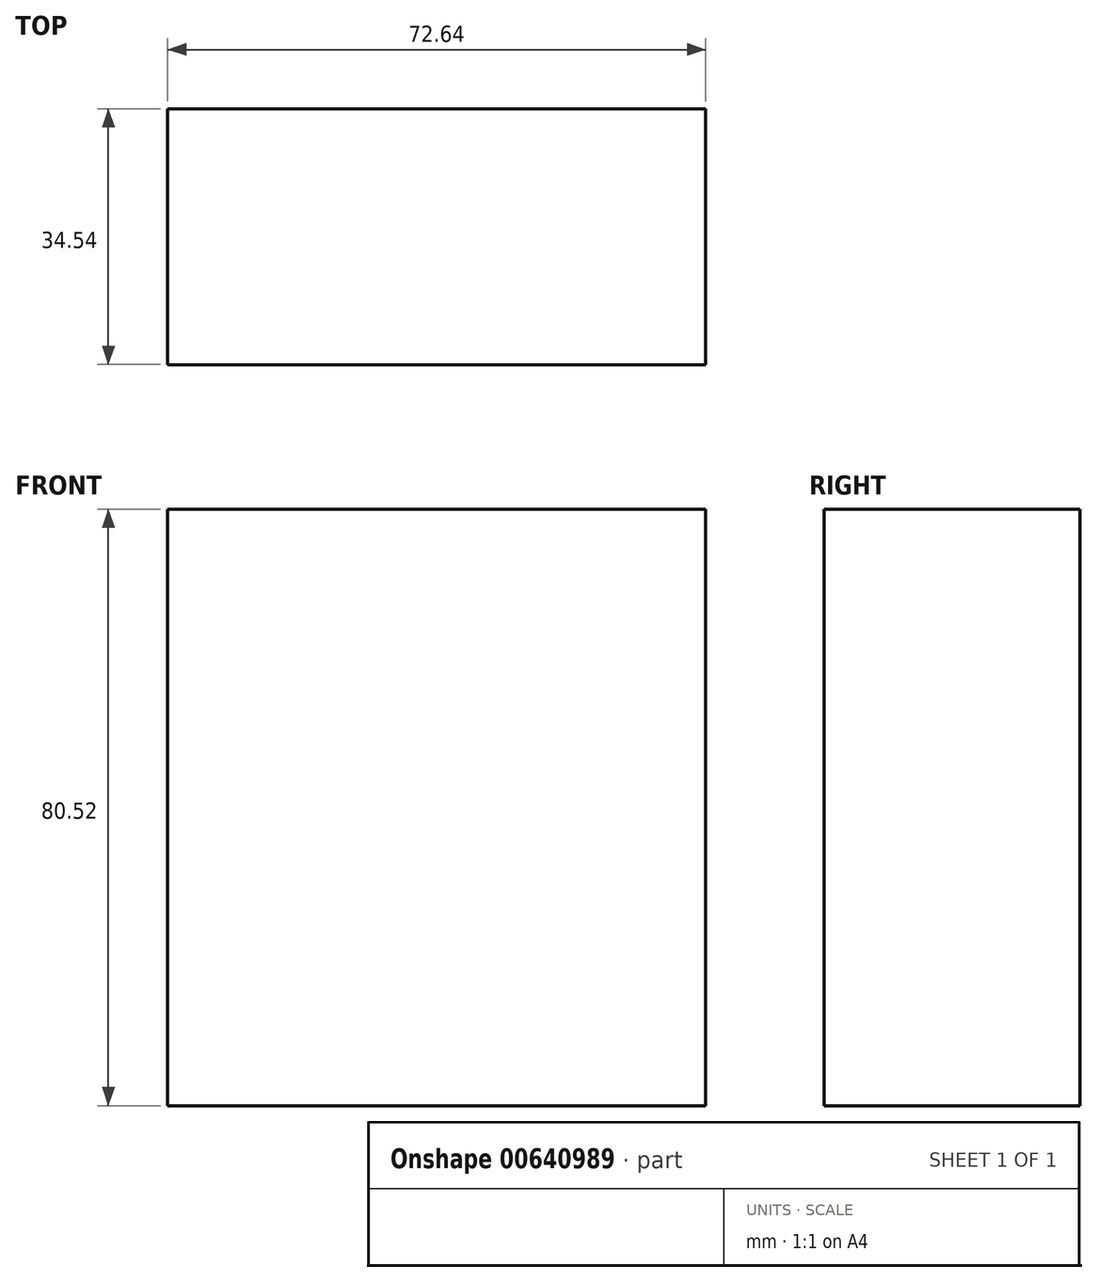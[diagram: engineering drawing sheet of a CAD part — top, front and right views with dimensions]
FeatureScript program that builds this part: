
annotation { "Feature Type Name" : "Feature", "Feature Type Description" : "" }
export const myFeature = defineFeature(function(context is Context, id is Id, definition is map)
    precondition{}
    {
        {
            var Q0;
            Q0=qCreatedBy(makeId("Front.planeOp"),FACE);
            var sketch = newSketch(context, id + "F0", { "sketchPlane" : qUnion([Q0])});
            skLineSegment(sketch, "E0.bottom", {"start": v(36.32, 40.26) * mm, "end": v(-36.32, 40.26) * mm});
            skLineSegment(sketch, "E0.top", {"start": v(36.32, -40.26) * mm, "end": v(-36.32, -40.26) * mm});
            skLineSegment(sketch, "E0.left", {"start": v(36.32, 40.26) * mm, "end": v(36.32, -40.26) * mm});
            skLineSegment(sketch, "E0.right", {"start": v(-36.32, 40.26) * mm, "end": v(-36.32, -40.26) * mm});
            skPoint(sketch, "E0.middle", {"position": v(0, 0) * mm});
            skSolve(sketch);
        }
        {
            var Q0;
            Q0=makeQuery(id+"F0.imprint","IMPRINT",FACE,{"disambiguationData":[TD([[makeQuery(id+"F0.imprint","IMPRINT",EDGE,{"derivedFrom":sQuery(id+"F0.wireOp",EDGE,"E0.bottom")}),1.0]])]});
            var Q1;
            Q1=sQuery(id+"F0.wireOp",EDGE,"E0.right");
            var Q2;
            Q2=sQuery(id+"F0.wireOp",EDGE,"E0.bottom");
            var Q3;
            Q3=sQuery(id+"F0.wireOp",EDGE,"E0.left");
            var Q4;
            Q4=sQuery(id+"F0.wireOp",EDGE,"E0.top");
            extrude(context, id + "F1", {"entities" : qUnion([Q0]), "surfaceEntities" : qUnion([Q1, Q2, Q3, Q4]), "depth" : 34.54 * mm, "offsetDistance" : 25.4 * mm});
        }
        {
            var Q0;
            Q0=qCreatedBy(makeId("Front.planeOp"),FACE);
            var sketch = newSketch(context, id + "F2", { "sketchPlane" : qUnion([Q0])});
            skCircle(sketch, "E1", {"center": v(0, 0) * mm, "radius": 23.38 * mm});
            skSolve(sketch);
        }
        {
            var Q0;
            Q0 = qSketchRegion(id + "F2", true);
            extrude(context, id + "F3", {"entities" : qUnion([Q0]), "operationType" : NewBodyOperationType.ADD, "depth" : 25.4 * mm, "offsetDistance" : 25.4 * mm});
        }
    });
